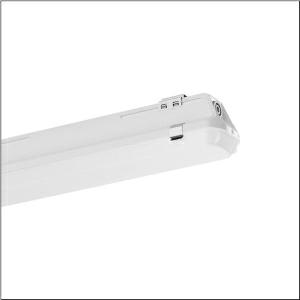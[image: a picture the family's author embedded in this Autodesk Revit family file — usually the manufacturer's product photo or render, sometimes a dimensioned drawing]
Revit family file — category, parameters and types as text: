
# Revit family: monsun_r__11_parking_51fg20dp440hhq_4cc6
name_source: partatom
category: Lighting Fixtures
units: mm (PartAtom-declared; Revit-internal decimal feet)

## family parameters
Cut with Voids When Loaded = No
Host = Face
Light Source = No
Part Type = Normal
Room Calculation Point = No
Round Connector Dimension = Use Diameter
Shared = No

## types (1)
- --- (1 x LED, 4840 lm, 31.3 W, 4000K)
    Apparent Load = 31 VA
    CIE Flux Codes = 45 75 93 94 100
    Color Rendering = 80
    Color Temperature = 4000K
    Default Elevation = 1800 mm
    Description = Monsun® 11 parking, damp-proof luminaire, chain hanger, primary optical cover: enclosure, of PC, light emission: direct distribution, primary light characteristic: symmetric, installation type: suspended mounting, surface-mounted, horizontal mounting, vertical mounting, LED, rated luminous flux: 4.840lm, luminous efficacy: 157lm/W, light colour: 840, colour temperature: 4000K, control gear: ECG DALI, with terminal, 5-pole, max. 2.5mm², mains connection: 220..240V, AC, 50/60Hz, rated input power: 31W, housing, of glass-fibre reinforced polyester, uncoated, bright grey, incl. chain hanger, length: 1.590mm, width: 90mm, height: 88mm, clip for enclosure, of stainless steel (V2A), ceiling mounting element, of stainless steel (V2A), chain hanger, of stainless steel (V2A), multi-sensor HC1, local controlcentral control, equipment: slave, scope of services: certified according to part 101,103,303,304, dimmable, protection rating (complete): IP66, insulation class (complete): insulation class I (protective earthing), certification: CE, ENEC, VDE, UKCA, protection symbol: D, impact resistance: IK08, permissible operating ambient temperature: -25..+40°C, standard: EN 50419, EN 60598-2-1, corresponds to IFS (International Featured Standards) requirements for safety and quality in the food industry, for indoor or canopied outdoor use, no direct snow, no direct sun, no direct rain, contact your sales advisor before using the luminaires in applications with unclear chemical exposure, large temperature fluctuations or condensation-forming humidity, LABS conformity tested according to VDMA 24364:2018-05, packaging unit: 1 piece
    Height = 89 mm
    Lamp = 1 x LED
    Lamp Light Flux = 4840 lm
    Lamp Power = 31.3 W
    Lamp count = 1
    Length = 1590 mm
    Luminous efficacy = 155 lm/W
    Manufacturer = Siteco
    ModVariant = No
    Model = 51FG20DP440HHQ
    Mounting Place = Ceiling
    Mounting Type = Surface mounted
    Number of Poles = 1
    OnlyDefault = Yes
    Power Factor = 1
    Product Name = Monsun® 11 parking
    Product group = damp-proof luminaire
    ProductGroupID = 300
    Protection Class = Protection class I
    Protection Degree = IP 66
    RLX_Detail_Level = 1
    RLX_Emergency_Light_Flux = 0 lm
    RLX_Emergency_Type = 0
    RLX_Emergency_Type_DB = No
    RlxData = <blob elided: 92277 chars, md5=1c071ce2>
    Socket = socket
    Standby Power = 0 W
    System Light Flux = 4840 lm
    System Power = 31 W
    Type Comments = factory setting: luminous flux: 100 % | dim-lin: 254 | 205 mA
    Type Image = l_1319650.jpg
    URL = http://relux.com
    VarID = @adj_113189
    Voltage = 0 V
    Weight = 0.00 kg
    Width = 90 mm

## geometry (parser evidence)
native form markers: Blend x4, Sweep x13
no freeform markers — native parametric forms only
